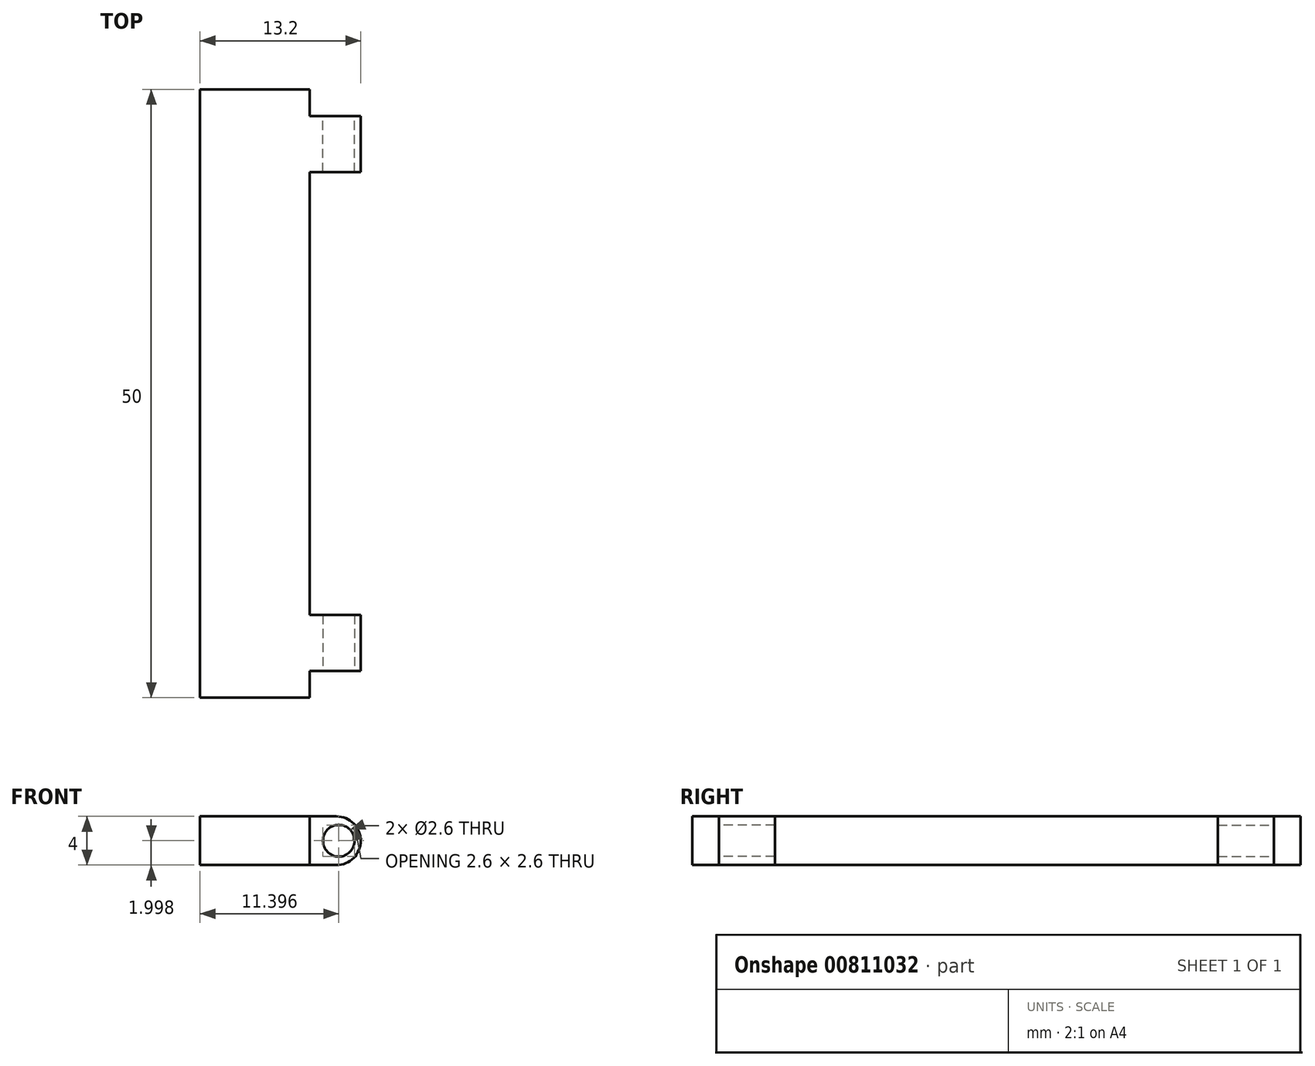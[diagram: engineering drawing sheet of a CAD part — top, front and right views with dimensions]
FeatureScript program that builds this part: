
annotation { "Feature Type Name" : "Feature", "Feature Type Description" : "" }
export const myFeature = defineFeature(function(context is Context, id is Id, definition is map)
    precondition{}
    {
        {
            var Q0;
            Q0=qCreatedBy(makeId("Front.planeOp"),FACE);
            var sketch = newSketch(context, id + "F0", { "sketchPlane" : qUnion([Q0])});
            skLineSegment(sketch, "E0.bottom", {"start": v(-27.37, 27.57) * mm, "end": v(-18.37, 27.57) * mm});
            skLineSegment(sketch, "E0.top", {"start": v(-27.37, 31.57) * mm, "end": v(-18.37, 31.57) * mm});
            skLineSegment(sketch, "E0.left", {"start": v(-27.37, 27.57) * mm, "end": v(-27.37, 31.57) * mm});
            skLineSegment(sketch, "E0.right", {"start": v(-18.37, 27.57) * mm, "end": v(-18.37, 31.57) * mm});
            skSolve(sketch);
        }
        {
            var Q0;
            Q0=qSketchRegion(id+"F0",true);
            extrude(context, id + "F1", {"entities" : qUnion([Q0]), "depth" : 25 * mm, "offsetDistance" : 25 * mm});
        }
        {
            var Q0;
            Q0=makeQuery(id+"F1.opExtrude","SWEPT_FACE",FACE,{"disambiguationData":[OSD([sQuery(id+"F0.wireOp",EDGE,"E0.right")])]});
            var sketch = newSketch(context, id + "F2", { "sketchPlane" : qUnion([Q0])});
            skLineSegment(sketch, "E1", {"start": v(-23, 31.57) * mm, "end": v(-23, 27.57) * mm, "construction": true});
            skLineSegment(sketch, "E2", {"start": v(-18, 31.57) * mm, "end": v(-18, 27.57) * mm, "construction": true});
            skLineSegment(sketch, "E3.bottom", {"start": v(-22.8, 31.57) * mm, "end": v(-18.2, 31.57) * mm});
            skLineSegment(sketch, "E3.top", {"start": v(-22.8, 27.57) * mm, "end": v(-18.2, 27.57) * mm});
            skLineSegment(sketch, "E3.left", {"start": v(-22.8, 31.57) * mm, "end": v(-22.8, 27.57) * mm});
            skLineSegment(sketch, "E3.right", {"start": v(-18.2, 31.57) * mm, "end": v(-18.2, 27.57) * mm});
            skSolve(sketch);
        }
        {
            var Q0;
            Q0=qSketchRegion(id+"F2",true);
            extrude(context, id + "F3", {"entities" : qUnion([Q0]), "operationType" : NewBodyOperationType.ADD, "depth" : 4.2 * mm, "offsetDistance" : 25 * mm});
        }
        {
            var Q0;
            Q0=makeQuery(id+"F3.opExtrude","SWEPT_FACE",FACE,{"disambiguationData":[OSD([sQuery(id+"F2.wireOp",EDGE,"E3.left")])]});
            var sketch = newSketch(context, id + "F4", { "sketchPlane" : qUnion([Q0])});
            skLineSegment(sketch, "E4", {"start": v(-18.37, 29.57) * mm, "end": v(-14.17, 29.57) * mm, "construction": true});
            skCircle(sketch, "E5", {"center": v(-15.97, 29.57) * mm, "radius": 1.3 * mm});
            skSolve(sketch);
        }
        {
            var Q0;
            Q0=qSketchRegion(id+"F4",true);
            extrude(context, id + "F5", {"entities" : qUnion([Q0]), "operationType" : NewBodyOperationType.REMOVE, "oppositeDirection" : true, "depth" : 25 * mm, "offsetDistance" : 25 * mm});
        }
        {
            var Q0;
            Q0=makeQuery(id+"F3.opExtrude","CAP_EDGE",EDGE,{"disambiguationData":[OSD([sQuery(id+"F2.wireOp",EDGE,"E3.bottom")])],"isStart":false});
            var Q1;
            Q1=makeQuery(id+"F3.opExtrude","CAP_EDGE",EDGE,{"disambiguationData":[OSD([sQuery(id+"F2.wireOp",EDGE,"E3.top")])],"isStart":false});
            fillet(context, id + "F6", {"entities" : qUnion([Q0, Q1]), "radius" : 2 * mm, "tangentPropagation" : true, "allowEdgeOverflow" : false});
        }
        {
            var Q0;
            Q0=makeQuery(id+"F1.opExtrude","SWEPT_BODY",BODY,{"disambiguationData":[OSD([sQuery(id+"F0.wireOp",EDGE,"E0.bottom"),sQuery(id+"F0.wireOp",EDGE,"E0.top"),sQuery(id+"F0.wireOp",EDGE,"E0.left"),sQuery(id+"F0.wireOp",EDGE,"E0.right")])]});
            var Q1;
            {var subQ0=makeQuery(id+"F1.opExtrude","CAP_FACE",FACE,{"disambiguationData":[OSD([sQuery(id+"F0.wireOp",EDGE,"E0.bottom"),sQuery(id+"F0.wireOp",EDGE,"E0.top"),sQuery(id+"F0.wireOp",EDGE,"E0.left"),sQuery(id+"F0.wireOp",EDGE,"E0.right")])],"isStart":true});Q1=makeQuery(id+"F8RuZVxz79B06aN_2.boolean.opBoolean","MERGE",FACE,{"derivedFrom":[subQ0,makeQuery(id+"F8RuZVxz79B06aN_2.opPattern","COPY",FACE,{"derivedFrom":subQ0,"instanceName":"1"})]});}
            mirror(context, id + "F7", {"operationType" : NewBodyOperationType.ADD, "entities" : qUnion([Q0]), "mirrorPlane" : qUnion([Q1])});
        }
        {
            var Q0;
            Q0=makeQuery(id+"F1.opExtrude","SWEPT_BODY",BODY,{"disambiguationData":[OSD([sQuery(id+"F0.wireOp",EDGE,"E0.bottom"),sQuery(id+"F0.wireOp",EDGE,"E0.top"),sQuery(id+"F0.wireOp",EDGE,"E0.left"),sQuery(id+"F0.wireOp",EDGE,"E0.right")])]});
            transform(context, id + "F8", {"entities" : qUnion([Q0]), "transformType" : TransformType.TRANSLATION_3D, "dx" : 0 * mm, "dy" : 0 * mm, "dz" : 0 * mm, "makeCopy" : true});
        }
        {
            var Q0;
            Q0=makeQuery(id+"F8.opPattern","COPY",BODY,{"derivedFrom":makeQuery(id+"F1.opExtrude","SWEPT_BODY",BODY,{"disambiguationData":[OSD([sQuery(id+"F0.wireOp",EDGE,"E0.bottom"),sQuery(id+"F0.wireOp",EDGE,"E0.top"),sQuery(id+"F0.wireOp",EDGE,"E0.left"),sQuery(id+"F0.wireOp",EDGE,"E0.right")])]}),"instanceName":"1"});
            deleteBodies(context, id + "F9", {"entities" : qUnion([Q0])});
        }
    });
